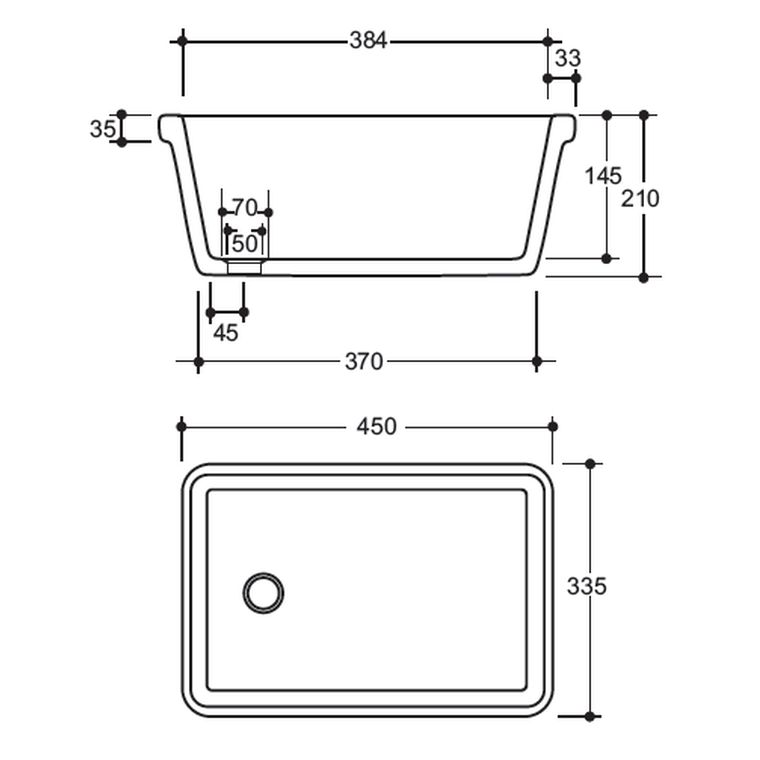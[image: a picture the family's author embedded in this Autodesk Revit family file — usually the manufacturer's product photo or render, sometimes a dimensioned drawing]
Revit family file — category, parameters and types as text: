
# Revit family: LIXIL - 234501WH - VAAL SINK LABORATORY
name_source: partatom
category: Plumbing Fixtures
units: mm (PartAtom-declared; Revit-internal decimal feet)

## family parameters
Always vertical = Yes
Cut with Voids When Loaded = No
Enable Cutting in Views = No
Maintain Annotation Orientation = No
OmniClass Number = 23.45.00.00
OmniClass Title = Sanitary, Laundry, and Cleaning Equipment
Part Type = Normal
Room Calculation Point = No
Round Connector Dimension = Use Diameter
Shared = Yes
Work Plane-Based = No

## types (1)
- 234501WH
    CW Connection Diameter = 0 mm  [stored 0 ft]
    CW Connection Radius = 0 mm  [stored 0 ft]
    Default Elevation = 0 mm  [stored 0 ft]
    Description = Vaal 450mm(w) x 335mm(d) x 210mm(h) SInk Laboratory basin to detail and spec. See sanware schedule. Available from Lixil.
    Hosted on lixil.co.za = https://www.lixil.co.za
    M _ BASIN = M _ LIXIL - VAAL - PORCELAIN - WHITE 01
    M _ POP UP WASTE = M _ LIXIL - STAINLESS STEEL 01
    Product Specification = Supplier: Lixil.
Product Description: Vaal Sanitaryware vitreous china 450x335x210mm rectangular laboratory sink without overflow and a centre end waste outlet.
10 Year Warranty Cobra Genuine Cobra TeamAssist Projects
Product Code: CLA43J43-2CO0344.
SKU Code	: 234501WH. 
Barcode: 6005826070385.
Brand: Vaal.
Range: Vaal.
Category: Kitchen.
Sub-Category: Sinks.
Material: Vitreous China. 
Colour: White.
Package Height: 240 mm
Package Width: 360 mm
Package Length: 470 mm
Product Height: 210 mm
Product Width: 450 mm
Product Length: 335 mm
Package Volume: 40608000 mm³.
Package Weight: 11.6 kg

Notes:
- Refer to manufacturer's and supplier's installation, maintenance and cleaning manual.
- Refer to manufacturer's and supplier's guarantees and warrantees document.
    Waste Connection Diameter = 45 mm  [stored 0.147638 ft]
    Waste Connection Radius = 23 mm

note: [stored X ft] marks values corroborated as IEEE doubles in the binary element streams (Revit-internal decimal feet)

## geometry (parser evidence)
native form markers: Sweep x13
no freeform markers — native parametric forms only
